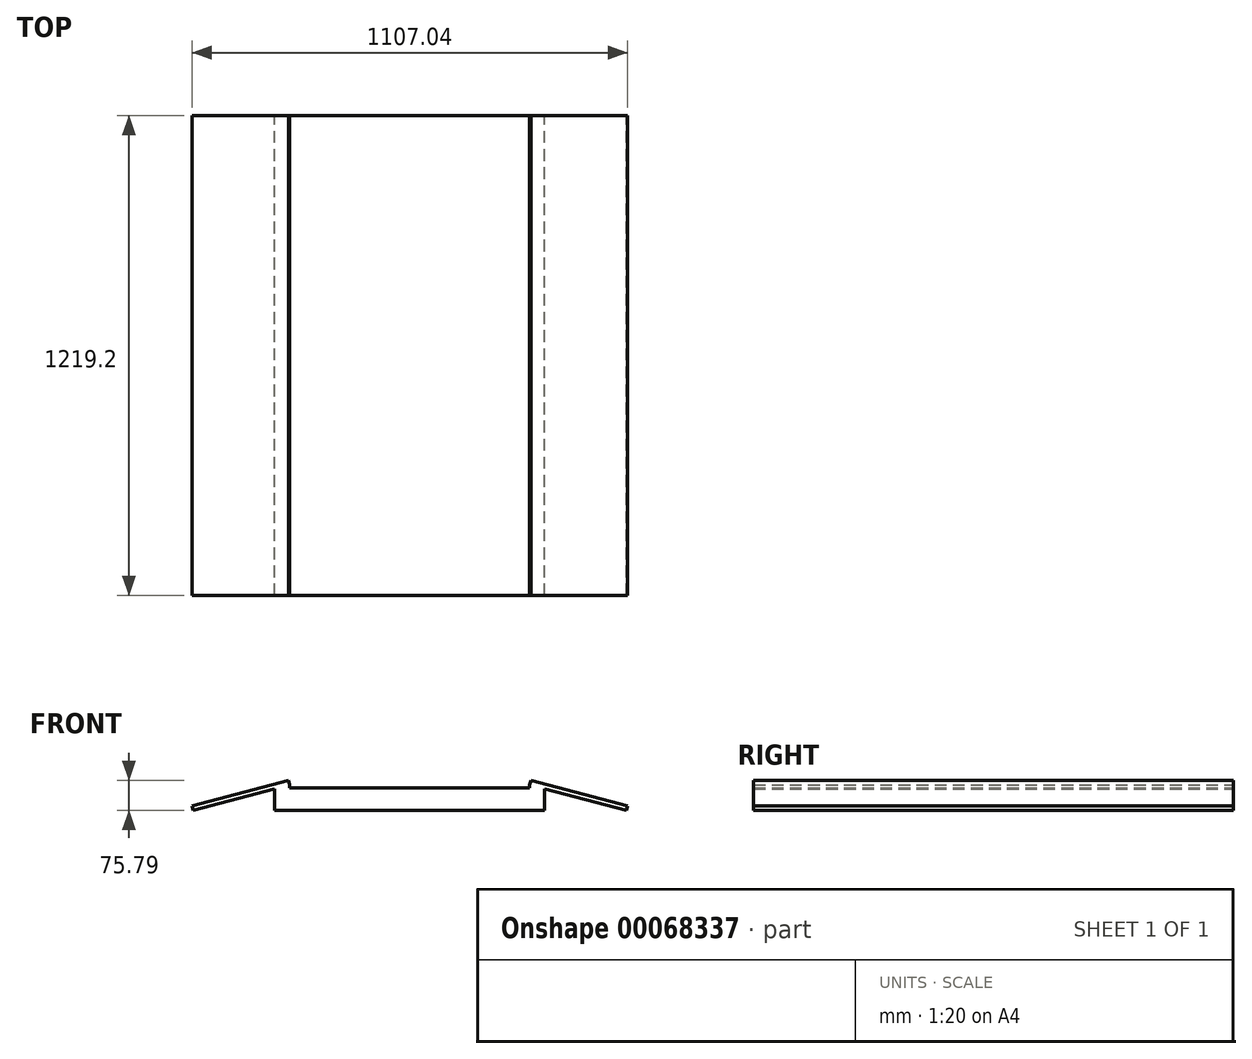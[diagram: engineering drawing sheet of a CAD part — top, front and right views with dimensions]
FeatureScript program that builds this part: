
annotation { "Feature Type Name" : "Feature", "Feature Type Description" : "" }
export const myFeature = defineFeature(function(context is Context, id is Id, definition is map)
    precondition{}
    {
        {
            var Q0;
            Q0=qCreatedBy(makeId("Front.planeOp"),FACE);
            var sketch = newSketch(context, id + "F0", { "sketchPlane" : qUnion([Q0])});
            skLineSegment(sketch, "E0", {"start": v(-304.8, 0) * mm, "end": v(304.8, 0) * mm});
            skLineSegment(sketch, "E1", {"start": v(304.8, 0) * mm, "end": v(-304.8, 0) * mm});
            skLineSegment(sketch, "E2", {"start": v(-304.8, -56.36) * mm, "end": v(-304.8, 0) * mm});
            skLineSegment(sketch, "E3", {"start": v(-304.8, -56.36) * mm, "end": v(304.8, -56.36) * mm});
            skLineSegment(sketch, "E4", {"start": v(304.8, -56.36) * mm, "end": v(304.8, 0) * mm});
            skLineSegment(sketch, "E5", {"start": v(-342.9, -1.95) * mm, "end": v(-342.9, -56.36) * mm});
            skLineSegment(sketch, "E6", {"start": v(-342.9, -56.36) * mm, "end": v(-304.8, -56.36) * mm});
            skLineSegment(sketch, "E7", {"start": v(-304.8, -56.36) * mm, "end": v(-304.8, 7.9) * mm});
            skLineSegment(sketch, "E8", {"start": v(-304.8, 7.9) * mm, "end": v(-342.9, -1.95) * mm});
            skLineSegment(sketch, "E9", {"start": v(-729.1, -56.36) * mm, "end": v(789.89, -56.36) * mm, "construction": true});
            skPoint(sketch, "E9.startSnap0", {"position": v(-323.85, -56.36) * mm});
            skLineSegment(sketch, "E10", {"start": v(-304.8, 7.9) * mm, "end": v(-307.78, 19.43) * mm});
            skLineSegment(sketch, "E11", {"start": v(-307.78, 19.43) * mm, "end": v(-553.52, -44.84) * mm});
            skLineSegment(sketch, "E12", {"start": v(-553.52, -44.84) * mm, "end": v(-550.5, -56.36) * mm});
            skLineSegment(sketch, "E13", {"start": v(-550.5, -56.36) * mm, "end": v(-304.8, 7.9) * mm});
            skLineSegment(sketch, "E14", {"start": v(0, 0) * mm, "end": v(0, 196.9) * mm, "construction": true});
            skLineSegment(sketch, "E15.MirrorCS", {"start": v(553.52, -44.84) * mm, "end": v(550.5, -56.36) * mm});
            skLineSegment(sketch, "E16.MirrorCS", {"start": v(342.9, -56.36) * mm, "end": v(304.8, -56.36) * mm});
            skLineSegment(sketch, "E17.MirrorCS", {"start": v(342.9, -1.95) * mm, "end": v(342.9, -56.36) * mm});
            skLineSegment(sketch, "E18.MirrorCS", {"start": v(304.8, 7.9) * mm, "end": v(342.9, -1.95) * mm});
            skLineSegment(sketch, "E19.MirrorCS", {"start": v(307.78, 19.43) * mm, "end": v(553.52, -44.84) * mm});
            skPoint(sketch, "E20.MirrorP", {"position": v(323.85, -56.36) * mm});
            skLineSegment(sketch, "E21.MirrorCS", {"start": v(729.1, -56.36) * mm, "end": v(-789.89, -56.36) * mm, "construction": true});
            skLineSegment(sketch, "E22.MirrorCS", {"start": v(550.5, -56.36) * mm, "end": v(304.8, 7.9) * mm});
            skLineSegment(sketch, "E23.MirrorCS", {"start": v(304.8, 7.9) * mm, "end": v(307.78, 19.43) * mm});
            skLineSegment(sketch, "E24.MirrorCS", {"start": v(304.8, -56.36) * mm, "end": v(304.8, 7.9) * mm});
            skSolve(sketch);
        }
        {
            var Q0;
            Q0 = qSketchRegion(id + "F0", true);
            extrude(context, id + "F1", {"entities" : qUnion([Q0]), "endBound" : BoundingType.SYMMETRIC, "depth" : 1219.2 * mm});
        }
    });
